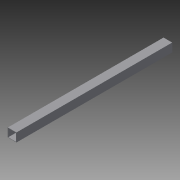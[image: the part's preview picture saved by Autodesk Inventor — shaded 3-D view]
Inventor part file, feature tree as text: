
AUTODESK INVENTOR PART (.ipt)
format: ipt  version: 2015 (Build 190159000, 159)  size: 74,752 bytes
history: native  units: in
note: dims shown in document units (in); Inventor stores cm internally (conversion verified against a paired STEP export)
features: extrude x1, sketch x1
ambient origin geometry x8: Origin, YZ Plane, XZ Plane, XY Plane, X Axis, Y Axis, Z Axis, Center Point
bodies: Solid1 (feature_tree)
feature tree (2):
  extrude  "Extrusion1"  Depth=2.0in
  sketch  "Sketch1"  dims[d0=2.0in d1=2.0in d2=0.083in d3=36.0in d4=0.0in]
